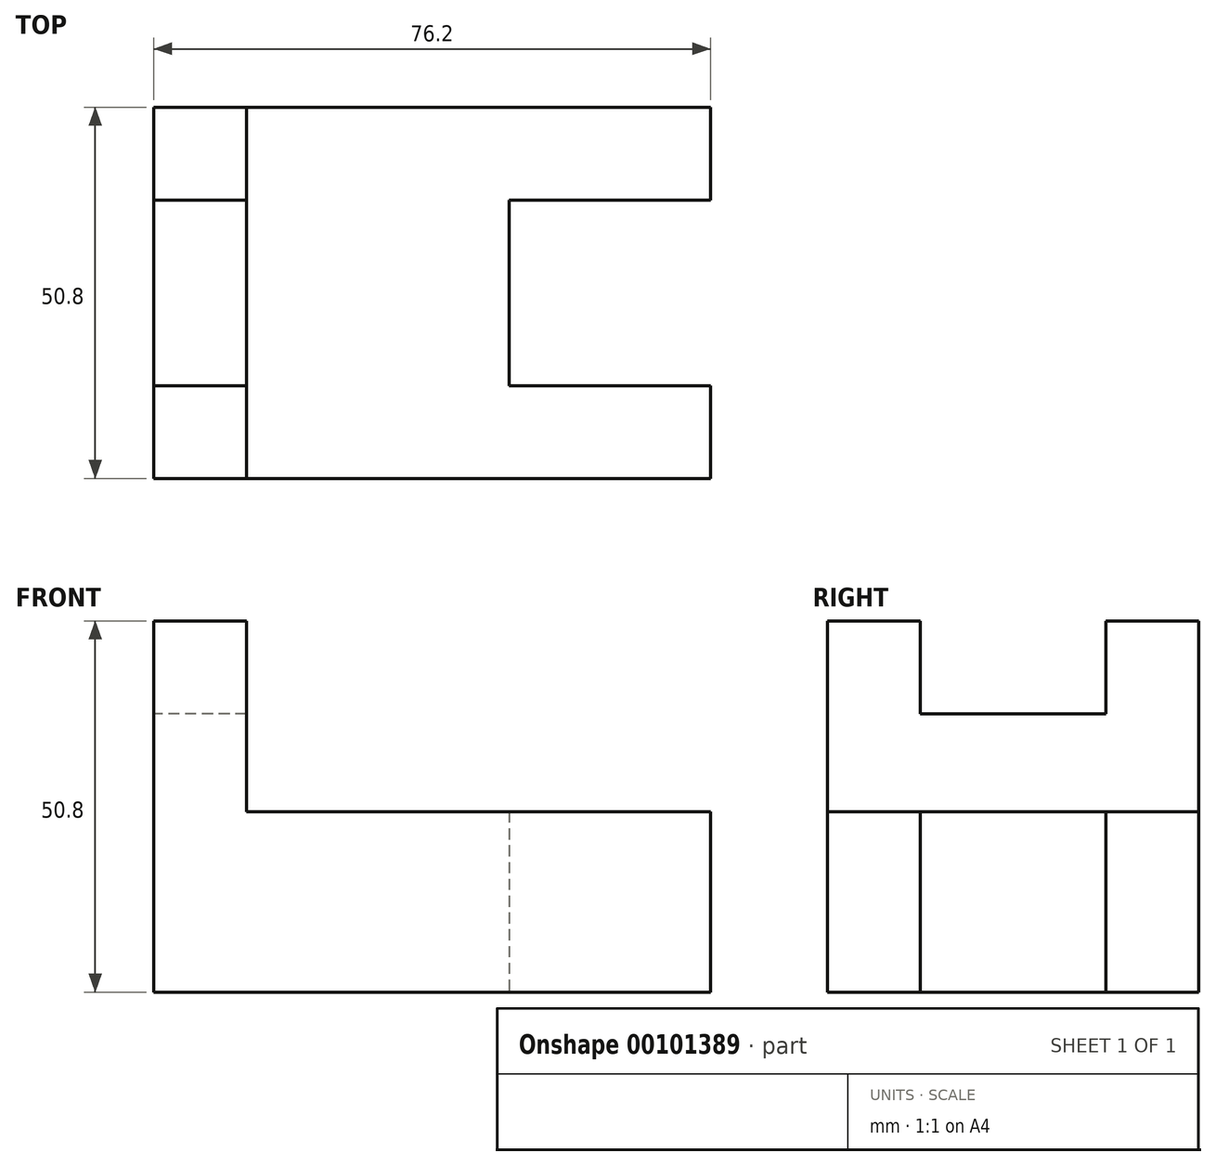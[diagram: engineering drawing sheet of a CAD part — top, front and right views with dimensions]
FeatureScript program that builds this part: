
annotation { "Feature Type Name" : "Feature", "Feature Type Description" : "" }
export const myFeature = defineFeature(function(context is Context, id is Id, definition is map)
    precondition{}
    {
        {
            var Q0;
            Q0=qCreatedBy(makeId("Front.planeOp"),FACE);
            var sketch = newSketch(context, id + "F0", { "sketchPlane" : qUnion([Q0])});
            skLineSegment(sketch, "E0", {"start": v(0, 0) * mm, "end": v(0, 50.8) * mm});
            skLineSegment(sketch, "E1", {"start": v(0, 50.8) * mm, "end": v(12.7, 50.8) * mm});
            skLineSegment(sketch, "E2", {"start": v(12.7, 50.8) * mm, "end": v(12.7, 24.69) * mm});
            skLineSegment(sketch, "E3", {"start": v(12.7, 24.69) * mm, "end": v(76.2, 24.69) * mm});
            skLineSegment(sketch, "E4", {"start": v(76.2, 24.69) * mm, "end": v(76.2, 0) * mm});
            skLineSegment(sketch, "E5", {"start": v(76.2, 0) * mm, "end": v(0, 0) * mm});
            skSolve(sketch);
        }
        {
            var Q0;
            Q0=qCreatedBy(makeId("Top.planeOp"),FACE);
            var sketch = newSketch(context, id + "F1", { "sketchPlane" : qUnion([Q0])});
            skLineSegment(sketch, "E6", {"start": v(76.2, 38.1) * mm, "end": v(48.63, 38.1) * mm});
            skLineSegment(sketch, "E7", {"start": v(48.63, 38.1) * mm, "end": v(48.63, 12.7) * mm});
            skLineSegment(sketch, "E8", {"start": v(48.63, 12.7) * mm, "end": v(76.2, 12.7) * mm});
            skLineSegment(sketch, "E9", {"start": v(76.2, 12.7) * mm, "end": v(76.2, 38.1) * mm});
            skSolve(sketch);
        }
        {
            var Q0;
            Q0=qCreatedBy(makeId("Right.planeOp"),FACE);
            var sketch = newSketch(context, id + "F2", { "sketchPlane" : qUnion([Q0])});
            skLineSegment(sketch, "E10", {"start": v(12.7, 50.8) * mm, "end": v(12.7, 38.1) * mm});
            skLineSegment(sketch, "E11", {"start": v(12.7, 38.1) * mm, "end": v(38.1, 38.1) * mm});
            skLineSegment(sketch, "E12", {"start": v(38.1, 38.1) * mm, "end": v(38.1, 50.8) * mm});
            skLineSegment(sketch, "E13", {"start": v(12.7, 50.8) * mm, "end": v(38.1, 50.8) * mm});
            skSolve(sketch);
        }
        {
            var Q0;
            Q0 = qSketchRegion(id + "F0", true);
            extrude(context, id + "F3", {"entities" : qUnion([Q0]), "oppositeDirection" : true, "depth" : 50.8 * mm});
        }
        {
            var Q0;
            Q0 = qSketchRegion(id + "F1", true);
            extrude(context, id + "F4", {"entities" : qUnion([Q0]), "operationType" : NewBodyOperationType.REMOVE, "depth" : 25.4 * mm});
        }
        {
            var Q0;
            Q0 = qSketchRegion(id + "F2", true);
            extrude(context, id + "F5", {"entities" : qUnion([Q0]), "operationType" : NewBodyOperationType.REMOVE, "depth" : 12.7 * mm});
        }
    });
